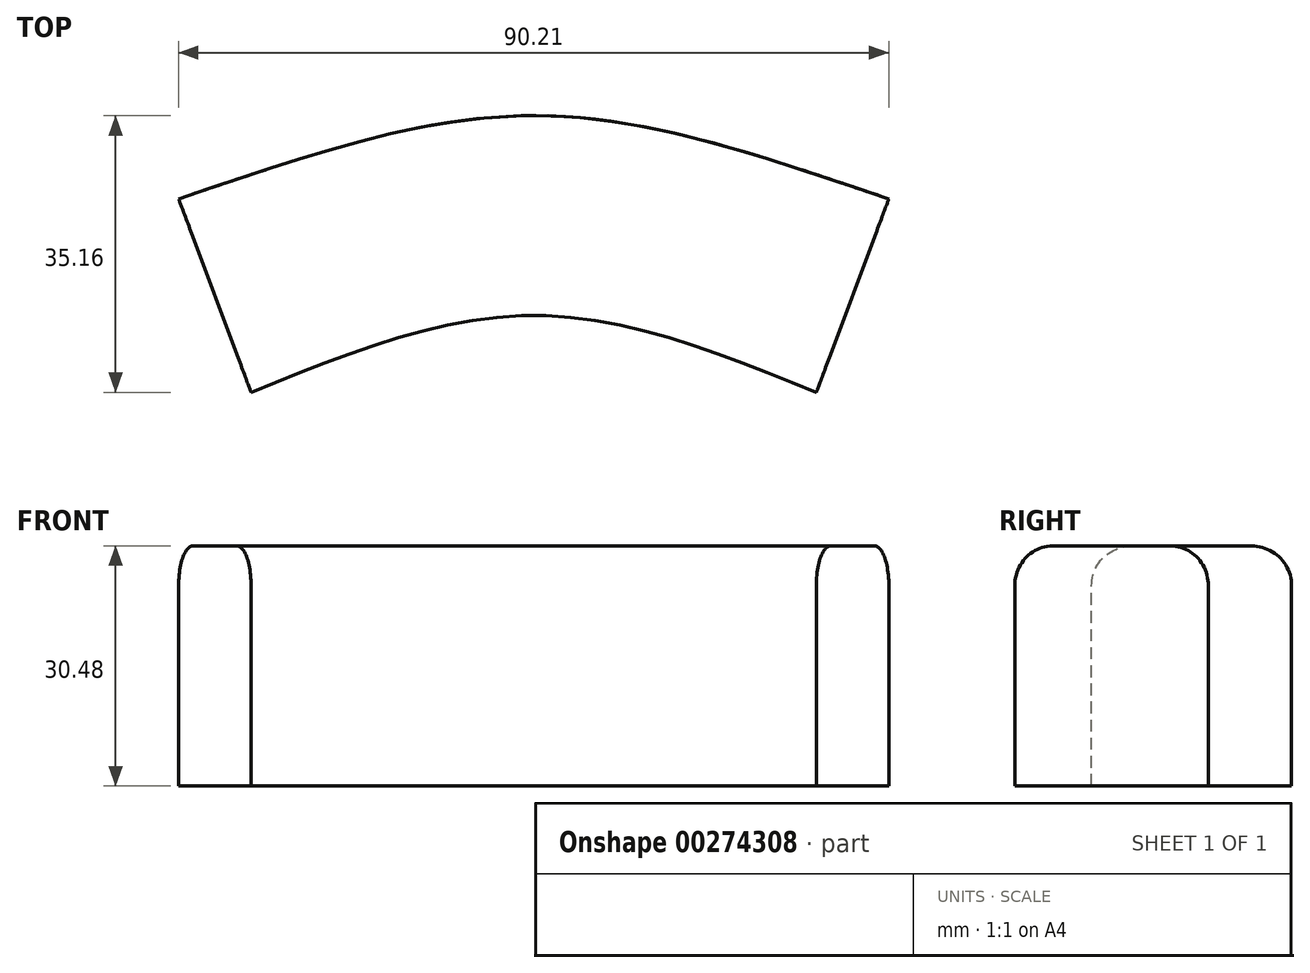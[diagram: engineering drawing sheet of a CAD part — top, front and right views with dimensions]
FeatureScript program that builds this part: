
annotation { "Feature Type Name" : "Feature", "Feature Type Description" : "" }
export const myFeature = defineFeature(function(context is Context, id is Id, definition is map)
    precondition{}
    {
        {
            var Q0;
            Q0=qCreatedBy(makeId("Top.planeOp"),FACE);
            var sketch = newSketch(context, id + "F0", { "sketchPlane" : qUnion([Q0])});
            skLineSegment(sketch, "E0", {"start": v(-41.11, -45.28) * mm, "end": v(-45.56, -33.38) * mm});
            skLineSegment(sketch, "E1", {"start": v(-41.11, -45.28) * mm, "end": v(-36.36, -57.98) * mm});
            skLineSegment(sketch, "E2.MirrorCS", {"start": v(40.2, -45.28) * mm, "end": v(35.45, -57.98) * mm});
            skLineSegment(sketch, "E3.MirrorCS", {"start": v(40.2, -45.28) * mm, "end": v(44.65, -33.38) * mm});
            skFitSpline(sketch, "E4", {"points": [v(-45.56, -33.38) * mm, v(-0.45, -22.82) * mm, v(44.65, -33.38) * mm], "startDerivative": vector(90.22, 30.01) * mm, "endDerivative": vector(90.22, -30.01) * mm});
            skFitSpline(sketch, "E5", {"points": [v(-36.36, -57.98) * mm, v(-0.45, -48.22) * mm, v(35.45, -57.98) * mm], "startDerivative": vector(71.8, 29.3) * mm, "endDerivative": vector(71.8, -29.3) * mm});
            skSolve(sketch);
        }
        {
            var Q0;
            Q0=makeQuery(id+"F0.imprint","IMPRINT",FACE,{"disambiguationData":[TD([[makeQuery(id+"F0.imprint","IMPRINT",EDGE,{"derivedFrom":sQuery(id+"F0.wireOp",EDGE,"E0")}),-1.0]])]});
            extrude(context, id + "F1", {"entities" : qUnion([Q0]), "depth" : 30.48 * mm});
        }
        {
            var Q0;
            Q0=makeQuery(id+"F1.opExtrude","CAP_EDGE",EDGE,{"disambiguationData":[OSD([sQuery(id+"F0.wireOp",EDGE,"E5")])],"isStart":false});
            var Q1;
            Q1=makeQuery(id+"F1.opExtrude","CAP_EDGE",EDGE,{"disambiguationData":[OSD([sQuery(id+"F0.wireOp",EDGE,"E4")])],"isStart":false});
            fillet(context, id + "F2", {"entities" : qUnion([Q0, Q1]), "radius" : 5.08 * mm, "tangentPropagation" : true, "allowEdgeOverflow" : false});
        }
    });
